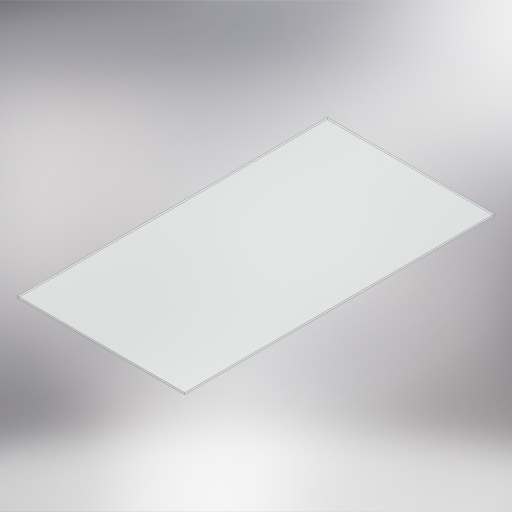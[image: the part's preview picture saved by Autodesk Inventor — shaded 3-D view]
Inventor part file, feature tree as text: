
AUTODESK INVENTOR PART (.ipt)
format: ipt  version: 2024 (Build 280153000, 153)  size: 317,440 bytes
history: native  units: in
note: dims shown in document units (in); Inventor stores cm internally (conversion verified against a paired STEP export)
features: extrude x1, sketch x1
ambient origin geometry x8: Origin, YZ Plane, XZ Plane, XY Plane, X Axis, Y Axis, Z Axis, Center Point
bodies: Solid1 (feature_tree)
feature tree (2):
  extrude  "Extrusion1"  Depth=0.9055in
  sketch  "Sketch1"  dims[d0=1.6772in d1=0.9055in d2=0.0098in d3=0.0in]
